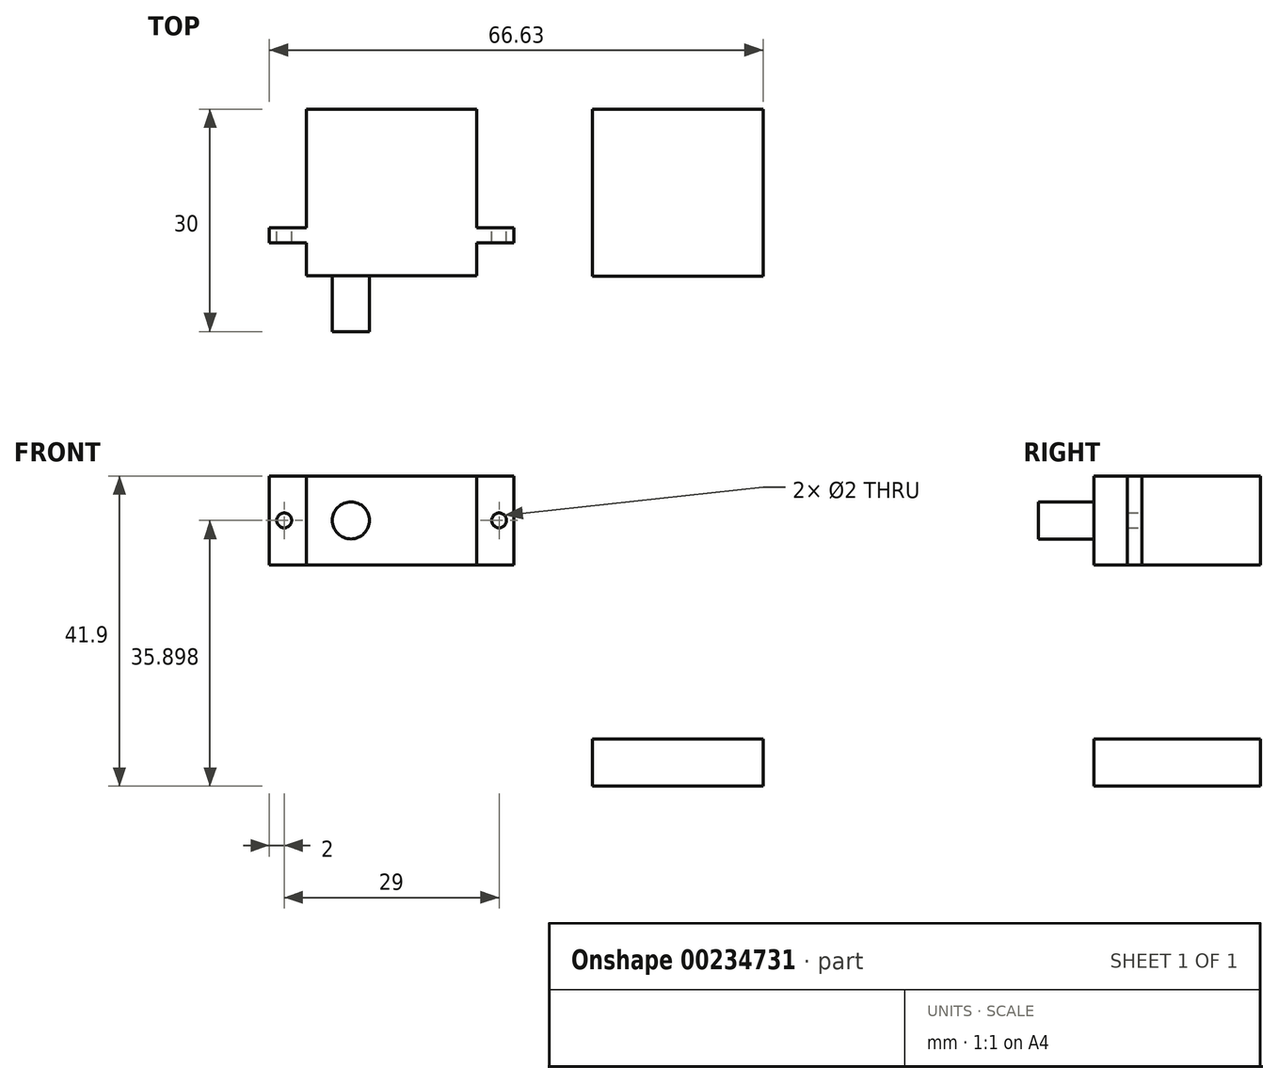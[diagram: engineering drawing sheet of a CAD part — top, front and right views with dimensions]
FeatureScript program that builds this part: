
annotation { "Feature Type Name" : "Feature", "Feature Type Description" : "" }
export const myFeature = defineFeature(function(context is Context, id is Id, definition is map)
    precondition{}
    {
        {
            var Q0;
            Q0=qCreatedBy(makeId("Front.planeOp"),FACE);
            var sketch = newSketch(context, id + "F0", { "sketchPlane" : qUnion([Q0])});
            skLineSegment(sketch, "E0.bottom", {"start": v(-25.38, 9.4) * mm, "end": v(-2.38, 9.4) * mm});
            skLineSegment(sketch, "E0.top", {"start": v(-25.38, -2.6) * mm, "end": v(-2.38, -2.6) * mm});
            skLineSegment(sketch, "E0.left", {"start": v(-25.38, 9.4) * mm, "end": v(-25.38, -2.6) * mm});
            skLineSegment(sketch, "E0.right", {"start": v(-2.38, 9.4) * mm, "end": v(-2.38, -2.6) * mm});
            skCircle(sketch, "E1", {"center": v(-19.38, 3.4) * mm, "radius": 2.5 * mm});
            skPoint(sketch, "E1.centerSnap0", {"position": v(-25.38, 3.4) * mm});
            skLineSegment(sketch, "E2.bottom", {"start": v(-30.38, 9.4) * mm, "end": v(-25.38, 9.4) * mm});
            skLineSegment(sketch, "E2.top", {"start": v(-30.38, -2.6) * mm, "end": v(-25.38, -2.6) * mm});
            skLineSegment(sketch, "E2.left", {"start": v(-30.38, 9.4) * mm, "end": v(-30.38, -2.6) * mm});
            skLineSegment(sketch, "E3.bottom", {"start": v(-2.38, 9.4) * mm, "end": v(2.62, 9.4) * mm});
            skLineSegment(sketch, "E3.top", {"start": v(-2.38, -2.6) * mm, "end": v(2.62, -2.6) * mm});
            skLineSegment(sketch, "E3.right", {"start": v(2.62, 9.4) * mm, "end": v(2.62, -2.6) * mm});
            skLineSegment(sketch, "E4.bottom", {"start": v(13.23, -26.09) * mm, "end": v(36.25, -26.09) * mm});
            skLineSegment(sketch, "E4.top", {"start": v(13.23, -32.49) * mm, "end": v(36.25, -32.49) * mm});
            skLineSegment(sketch, "E4.left", {"start": v(13.23, -26.09) * mm, "end": v(13.23, -32.49) * mm});
            skLineSegment(sketch, "E4.right", {"start": v(36.25, -26.09) * mm, "end": v(36.25, -32.49) * mm});
            skLineSegment(sketch, "E5", {"start": v(-25.38, 3.4) * mm, "end": v(-30.38, 3.4) * mm});
            skLineSegment(sketch, "E6", {"start": v(-2.38, 3.4) * mm, "end": v(2.62, 3.4) * mm});
            skCircle(sketch, "E7", {"center": v(-28.38, 3.4) * mm, "radius": 1 * mm});
            skCircle(sketch, "E8", {"center": v(0.62, 3.4) * mm, "radius": 1 * mm});
            skSolve(sketch);
        }
        {
            var Q0;
            Q0=makeQuery(id+"F0.imprint","IMPRINT",FACE,{"disambiguationData":[TD([[makeQuery(id+"F0.imprint","IMPRINT",EDGE,{"derivedFrom":sQuery(id+"F0.wireOp",EDGE,"E1")}),1.0]])]});
            extrude(context, id + "F1", {"entities" : qUnion([Q0]), "depth" : 30 * mm});
        }
        {
            var Q0;
            Q0=makeQuery(id+"F0.imprint","IMPRINT",FACE,{"disambiguationData":[TD([[makeQuery(id+"F0.imprint","IMPRINT",EDGE,{"derivedFrom":sQuery(id+"F0.wireOp",EDGE,"E0.bottom")}),-1.0]])]});
            extrude(context, id + "F2", {"entities" : qUnion([Q0]), "operationType" : NewBodyOperationType.ADD, "depth" : 22.5 * mm});
        }
        {
            var Q0;
            Q0=makeQuery(id+"F0.imprint","IMPRINT",FACE,{"disambiguationData":[TD([[makeQuery(id+"F0.imprint","IMPRINT",EDGE,{"derivedFrom":sQuery(id+"F0.wireOp",EDGE,"E3.bottom")}),-1.0]])]});
            var Q1;
            Q1=makeQuery(id+"F0.imprint","IMPRINT",FACE,{"disambiguationData":[TD([[makeQuery(id+"F0.imprint","IMPRINT",EDGE,{"derivedFrom":sQuery(id+"F0.wireOp",EDGE,"E2.bottom")}),-1.0]])]});
            var Q2;
            {var subQ1=sQuery(id+"F0.wireOp",EDGE,"E2.top");Q2=makeQuery(id+"F0.imprint","IMPRINT",FACE,{"disambiguationData":[TD([[makeQuery(id+"F0.imprint","IMPRINT",EDGE,{"derivedFrom":subQ1}),1.0]])]});}
            var Q3;
            {var subQ6=sQuery(id+"F0.wireOp",EDGE,"E3.top");Q3=makeQuery(id+"F0.imprint","IMPRINT",FACE,{"disambiguationData":[TD([[makeQuery(id+"F0.imprint","IMPRINT",EDGE,{"derivedFrom":subQ6}),1.0]])]});}
            extrude(context, id + "F3", {"entities" : qUnion([Q0, Q1, Q2, Q3]), "operationType" : NewBodyOperationType.ADD, "offsetDistance" : 25 * mm, "depth" : 18 * mm, "hasSecondDirection" : true, "secondDirectionOppositeDirection" : true, "secondDirectionDepth" : -16 * mm});
        }
        {
            var Q0;
            Q0=makeQuery(id+"F0.imprint","IMPRINT",FACE,{"disambiguationData":[TD([[makeQuery(id+"F0.imprint","IMPRINT",EDGE,{"derivedFrom":sQuery(id+"F0.wireOp",EDGE,"E4.bottom")}),-1.0]])]});
            extrude(context, id + "F4", {"entities" : qUnion([Q0]), "depth" : 22.5 * mm});
        }
    });
